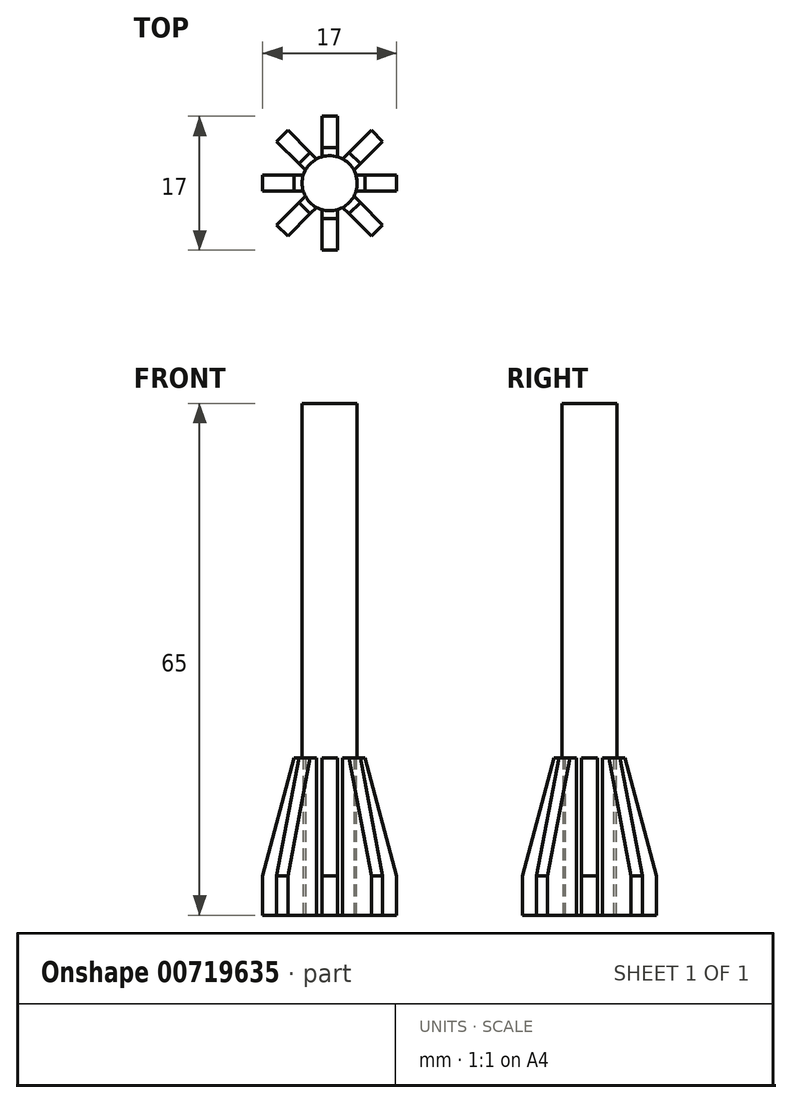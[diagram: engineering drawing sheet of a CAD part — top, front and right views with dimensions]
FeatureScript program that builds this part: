
annotation { "Feature Type Name" : "Feature", "Feature Type Description" : "" }
export const myFeature = defineFeature(function(context is Context, id is Id, definition is map)
    precondition{}
    {
        {
            var Q0;
            Q0=qCreatedBy(makeId("Top.planeOp"),FACE);
            var sketch = newSketch(context, id + "F0", { "sketchPlane" : qUnion([Q0])});
            skLineSegment(sketch, "E0.bottom", {"start": v(4.78, 10.23) * mm, "end": v(-7.24, -1.79) * mm});
            skLineSegment(sketch, "E0.top", {"start": v(6.2, 8.82) * mm, "end": v(-5.83, -3.2) * mm});
            skLineSegment(sketch, "E0.left", {"start": v(4.78, 10.23) * mm, "end": v(6.2, 8.82) * mm});
            skLineSegment(sketch, "E0.right", {"start": v(-7.24, -1.79) * mm, "end": v(-5.83, -3.2) * mm});
            skPoint(sketch, "E0.middle", {"position": v(-0.52, 3.52) * mm});
            skLineSegment(sketch, "E1.bottom", {"start": v(-5.83, 10.23) * mm, "end": v(-7.24, 8.82) * mm});
            skLineSegment(sketch, "E1.top", {"start": v(6.2, -1.79) * mm, "end": v(4.78, -3.2) * mm});
            skLineSegment(sketch, "E1.left", {"start": v(-5.83, 10.23) * mm, "end": v(6.2, -1.79) * mm});
            skLineSegment(sketch, "E1.right", {"start": v(-7.24, 8.82) * mm, "end": v(4.78, -3.2) * mm});
            skCircle(sketch, "E2", {"center": v(-0.52, 3.52) * mm, "radius": 3.5 * mm});
            skLineSegment(sketch, "E3.bottom", {"start": v(0.48, 12.02) * mm, "end": v(-1.52, 12.02) * mm});
            skLineSegment(sketch, "E3.top", {"start": v(0.48, -4.98) * mm, "end": v(-1.52, -4.98) * mm});
            skLineSegment(sketch, "E3.left", {"start": v(0.48, 12.02) * mm, "end": v(0.48, -4.98) * mm});
            skLineSegment(sketch, "E3.right", {"start": v(-1.52, 12.02) * mm, "end": v(-1.52, -4.98) * mm});
            skLineSegment(sketch, "E4.bottom", {"start": v(7.98, 4.52) * mm, "end": v(-9.02, 4.52) * mm});
            skLineSegment(sketch, "E4.top", {"start": v(7.98, 2.52) * mm, "end": v(-9.02, 2.52) * mm});
            skLineSegment(sketch, "E4.left", {"start": v(7.98, 4.52) * mm, "end": v(7.98, 2.52) * mm});
            skLineSegment(sketch, "E4.right", {"start": v(-9.02, 4.52) * mm, "end": v(-9.02, 2.52) * mm});
            skSolve(sketch);
        }
        {
            var Q0;
            {var subQ0=sQuery(id+"F0.wireOp",EDGE,"E2");var subQ1=sQuery(id+"F0.wireOp",EDGE,"E0.bottom");var subQ2=makeQuery(id+"F0.imprint","INTERSECT",VERTEX,{"disambiguationData":[OD(0.0)],"derivedFrom":[subQ1,subQ0]});Q0=makeQuery(id+"F0.imprint","IMPRINT",FACE,{"disambiguationData":[TD([[makeQuery(id+"F0.imprint","IMPRINT",EDGE,{"disambiguationData":[TD([[subQ2,-1.0]])],"derivedFrom":subQ1}),-1.0]])]});}
            var Q1;
            {var subQ0=sQuery(id+"F0.wireOp",EDGE,"E2");var subQ1=sQuery(id+"F0.wireOp",EDGE,"E0.bottom");var subQ2=makeQuery(id+"F0.imprint","INTERSECT",VERTEX,{"disambiguationData":[OD(1.0)],"derivedFrom":[subQ1,subQ0]});Q1=makeQuery(id+"F0.imprint","IMPRINT",FACE,{"disambiguationData":[TD([[makeQuery(id+"F0.imprint","IMPRINT",EDGE,{"disambiguationData":[TD([[subQ2,1.0]])],"derivedFrom":subQ1}),-1.0]])]});}
            var Q2;
            {var subQ0=sQuery(id+"F0.wireOp",EDGE,"E2");var subQ1=sQuery(id+"F0.wireOp",EDGE,"E0.top");var subQ2=makeQuery(id+"F0.imprint","INTERSECT",VERTEX,{"disambiguationData":[OD(0.0)],"derivedFrom":[subQ1,subQ0]});Q2=makeQuery(id+"F0.imprint","IMPRINT",FACE,{"disambiguationData":[TD([[makeQuery(id+"F0.imprint","IMPRINT",EDGE,{"disambiguationData":[TD([[subQ2,-1.0]])],"derivedFrom":subQ1}),1.0]])]});}
            var Q3;
            {var subQ0=sQuery(id+"F0.wireOp",EDGE,"E2");var subQ1=sQuery(id+"F0.wireOp",EDGE,"E0.top");var subQ2=makeQuery(id+"F0.imprint","INTERSECT",VERTEX,{"disambiguationData":[OD(1.0)],"derivedFrom":[subQ1,subQ0]});Q3=makeQuery(id+"F0.imprint","IMPRINT",FACE,{"disambiguationData":[TD([[makeQuery(id+"F0.imprint","IMPRINT",EDGE,{"disambiguationData":[TD([[subQ2,1.0]])],"derivedFrom":subQ1}),1.0]])]});}
            var Q4;
            {var subQ1=sQuery(id+"F0.wireOp",EDGE,"E0.bottom");var subQ5=sQuery(id+"F0.wireOp",EDGE,"E2");var subQ6=makeQuery(id+"F0.imprint","INTERSECT",VERTEX,{"disambiguationData":[OD(0.0)],"derivedFrom":[subQ1,subQ5]});Q4=makeQuery(id+"F0.imprint","IMPRINT",FACE,{"disambiguationData":[TD([[makeQuery(id+"F0.imprint","IMPRINT",EDGE,{"disambiguationData":[TD([[subQ6,-1.0]])],"derivedFrom":subQ1}),1.0]])]});}
            var Q5;
            {var subQ0=sQuery(id+"F0.wireOp",EDGE,"E1.left");var subQ1=sQuery(id+"F0.wireOp",EDGE,"E0.bottom");var subQ2=makeQuery(id+"F0.imprint","INTERSECT",VERTEX,{"derivedFrom":[subQ1,subQ0]});Q5=makeQuery(id+"F0.imprint","IMPRINT",FACE,{"disambiguationData":[TD([[makeQuery(id+"F0.imprint","IMPRINT",EDGE,{"disambiguationData":[TD([[subQ2,-1.0]])],"derivedFrom":subQ1}),-1.0]])]});}
            var Q6;
            {var subQ5=sQuery(id+"F0.wireOp",EDGE,"E2");var subQ6=sQuery(id+"F0.wireOp",EDGE,"E0.bottom");var subQ7=makeQuery(id+"F0.imprint","INTERSECT",VERTEX,{"disambiguationData":[OD(1.0)],"derivedFrom":[subQ6,subQ5]});Q6=makeQuery(id+"F0.imprint","IMPRINT",FACE,{"disambiguationData":[TD([[makeQuery(id+"F0.imprint","IMPRINT",EDGE,{"disambiguationData":[TD([[subQ7,1.0]])],"derivedFrom":subQ6}),1.0]])]});}
            var Q7;
            {var subQ0=sQuery(id+"F0.wireOp",EDGE,"E1.left");var subQ1=sQuery(id+"F0.wireOp",EDGE,"E0.top");var subQ2=makeQuery(id+"F0.imprint","INTERSECT",VERTEX,{"derivedFrom":[subQ1,subQ0]});Q7=makeQuery(id+"F0.imprint","IMPRINT",FACE,{"disambiguationData":[TD([[makeQuery(id+"F0.imprint","IMPRINT",EDGE,{"disambiguationData":[TD([[subQ2,-1.0]])],"derivedFrom":subQ1}),1.0]])]});}
            var Q8;
            {var subQ0=sQuery(id+"F0.wireOp",EDGE,"E1.left");var subQ1=sQuery(id+"F0.wireOp",EDGE,"E0.bottom");var subQ2=makeQuery(id+"F0.imprint","INTERSECT",VERTEX,{"derivedFrom":[subQ1,subQ0]});Q8=makeQuery(id+"F0.imprint","IMPRINT",FACE,{"disambiguationData":[TD([[makeQuery(id+"F0.imprint","IMPRINT",EDGE,{"disambiguationData":[TD([[subQ2,-1.0]])],"derivedFrom":subQ1}),1.0]])]});}
            var Q9;
            {var subQ1=sQuery(id+"F0.wireOp",EDGE,"E1.left");var subQ5=sQuery(id+"F0.wireOp",EDGE,"E2");var subQ9=makeQuery(id+"F0.imprint","INTERSECT",VERTEX,{"disambiguationData":[OD(0.0)],"derivedFrom":[subQ1,subQ5]});Q9=makeQuery(id+"F0.imprint","IMPRINT",FACE,{"disambiguationData":[TD([[makeQuery(id+"F0.imprint","IMPRINT",EDGE,{"disambiguationData":[TD([[subQ9,-1.0]])],"derivedFrom":subQ1}),-1.0]])]});}
            var Q10;
            {var subQ0=sQuery(id+"F0.wireOp",EDGE,"E3.left");var subQ1=sQuery(id+"F0.wireOp",EDGE,"E0.top");var subQ2=makeQuery(id+"F0.imprint","INTERSECT",VERTEX,{"derivedFrom":[subQ1,subQ0]});Q10=makeQuery(id+"F0.imprint","IMPRINT",FACE,{"disambiguationData":[TD([[makeQuery(id+"F0.imprint","IMPRINT",EDGE,{"disambiguationData":[TD([[subQ2,-1.0]])],"derivedFrom":subQ1}),1.0]])]});}
            var Q11;
            {var subQ5=sQuery(id+"F0.wireOp",EDGE,"E1.right");var subQ7=sQuery(id+"F0.wireOp",EDGE,"E0.bottom");var subQ8=makeQuery(id+"F0.imprint","INTERSECT",VERTEX,{"derivedFrom":[subQ7,subQ5]});Q11=makeQuery(id+"F0.imprint","IMPRINT",FACE,{"disambiguationData":[TD([[makeQuery(id+"F0.imprint","IMPRINT",EDGE,{"disambiguationData":[TD([[subQ8,-1.0]])],"derivedFrom":subQ7}),-1.0]])]});}
            var Q12;
            {var subQ0=sQuery(id+"F0.wireOp",EDGE,"E3.left");var subQ5=sQuery(id+"F0.wireOp",EDGE,"E0.bottom");var subQ6=makeQuery(id+"F0.imprint","INTERSECT",VERTEX,{"derivedFrom":[subQ5,subQ0]});Q12=makeQuery(id+"F0.imprint","IMPRINT",FACE,{"disambiguationData":[TD([[makeQuery(id+"F0.imprint","IMPRINT",EDGE,{"disambiguationData":[TD([[subQ6,-1.0]])],"derivedFrom":subQ5}),-1.0]])]});}
            var Q13;
            {var subQ0=sQuery(id+"F0.wireOp",EDGE,"E4.bottom");var subQ3=sQuery(id+"F0.wireOp",EDGE,"E0.top");var subQ4=makeQuery(id+"F0.imprint","INTERSECT",VERTEX,{"derivedFrom":[subQ3,subQ0]});Q13=makeQuery(id+"F0.imprint","IMPRINT",FACE,{"disambiguationData":[TD([[makeQuery(id+"F0.imprint","IMPRINT",EDGE,{"disambiguationData":[TD([[subQ4,-1.0]])],"derivedFrom":subQ3}),1.0]])]});}
            var Q14;
            {var subQ0=sQuery(id+"F0.wireOp",EDGE,"E3.right");var subQ1=sQuery(id+"F0.wireOp",EDGE,"E0.bottom");var subQ2=makeQuery(id+"F0.imprint","INTERSECT",VERTEX,{"derivedFrom":[subQ1,subQ0]});Q14=makeQuery(id+"F0.imprint","IMPRINT",FACE,{"disambiguationData":[TD([[makeQuery(id+"F0.imprint","IMPRINT",EDGE,{"disambiguationData":[TD([[subQ2,-1.0]])],"derivedFrom":subQ1}),1.0]])]});}
            var Q15;
            {var subQ0=sQuery(id+"F0.wireOp",EDGE,"E3.left");var subQ1=sQuery(id+"F0.wireOp",EDGE,"E0.bottom");var subQ2=makeQuery(id+"F0.imprint","INTERSECT",VERTEX,{"derivedFrom":[subQ1,subQ0]});Q15=makeQuery(id+"F0.imprint","IMPRINT",FACE,{"disambiguationData":[TD([[makeQuery(id+"F0.imprint","IMPRINT",EDGE,{"disambiguationData":[TD([[subQ2,-1.0]])],"derivedFrom":subQ1}),1.0]])]});}
            var Q16;
            {var subQ0=sQuery(id+"F0.wireOp",EDGE,"E4.bottom");var subQ1=sQuery(id+"F0.wireOp",EDGE,"E0.bottom");var subQ2=makeQuery(id+"F0.imprint","INTERSECT",VERTEX,{"derivedFrom":[subQ1,subQ0]});Q16=makeQuery(id+"F0.imprint","IMPRINT",FACE,{"disambiguationData":[TD([[makeQuery(id+"F0.imprint","IMPRINT",EDGE,{"disambiguationData":[TD([[subQ2,-1.0]])],"derivedFrom":subQ1}),-1.0]])]});}
            var Q17;
            {var subQ0=sQuery(id+"F0.wireOp",EDGE,"E2");var subQ1=sQuery(id+"F0.wireOp",EDGE,"E1.left");var subQ2=makeQuery(id+"F0.imprint","INTERSECT",VERTEX,{"disambiguationData":[OD(1.0)],"derivedFrom":[subQ1,subQ0]});Q17=makeQuery(id+"F0.imprint","IMPRINT",FACE,{"disambiguationData":[TD([[makeQuery(id+"F0.imprint","IMPRINT",EDGE,{"disambiguationData":[TD([[subQ2,1.0]])],"derivedFrom":subQ1}),-1.0]])]});}
            var Q18;
            {var subQ0=sQuery(id+"F0.wireOp",EDGE,"E1.left");var subQ1=sQuery(id+"F0.wireOp",EDGE,"E0.top");var subQ2=makeQuery(id+"F0.imprint","INTERSECT",VERTEX,{"derivedFrom":[subQ1,subQ0]});Q18=makeQuery(id+"F0.imprint","IMPRINT",FACE,{"disambiguationData":[TD([[makeQuery(id+"F0.imprint","IMPRINT",EDGE,{"disambiguationData":[TD([[subQ2,-1.0]])],"derivedFrom":subQ1}),-1.0]])]});}
            var Q19;
            {var subQ9=sQuery(id+"F0.wireOp",EDGE,"E4.bottom");var subQ13=sQuery(id+"F0.wireOp",EDGE,"E0.bottom");var subQ14=makeQuery(id+"F0.imprint","INTERSECT",VERTEX,{"derivedFrom":[subQ13,subQ9]});Q19=makeQuery(id+"F0.imprint","IMPRINT",FACE,{"disambiguationData":[TD([[makeQuery(id+"F0.imprint","IMPRINT",EDGE,{"disambiguationData":[TD([[subQ14,-1.0]])],"derivedFrom":subQ13}),1.0]])]});}
            var Q20;
            {var subQ0=sQuery(id+"F0.wireOp",EDGE,"E2");var subQ1=sQuery(id+"F0.wireOp",EDGE,"E1.left");var subQ2=makeQuery(id+"F0.imprint","INTERSECT",VERTEX,{"disambiguationData":[OD(1.0)],"derivedFrom":[subQ1,subQ0]});Q20=makeQuery(id+"F0.imprint","IMPRINT",FACE,{"disambiguationData":[TD([[makeQuery(id+"F0.imprint","IMPRINT",EDGE,{"disambiguationData":[TD([[subQ2,1.0]])],"derivedFrom":subQ1}),1.0]])]});}
            var Q21;
            {var subQ0=sQuery(id+"F0.wireOp",EDGE,"E4.bottom");var subQ1=sQuery(id+"F0.wireOp",EDGE,"E1.left");var subQ2=makeQuery(id+"F0.imprint","INTERSECT",VERTEX,{"derivedFrom":[subQ1,subQ0]});Q21=makeQuery(id+"F0.imprint","IMPRINT",FACE,{"disambiguationData":[TD([[makeQuery(id+"F0.imprint","IMPRINT",EDGE,{"disambiguationData":[TD([[subQ2,-1.0]])],"derivedFrom":subQ1}),1.0]])]});}
            var Q22;
            {var subQ0=sQuery(id+"F0.wireOp",EDGE,"E3.right");var subQ1=sQuery(id+"F0.wireOp",EDGE,"E0.bottom");var subQ2=makeQuery(id+"F0.imprint","INTERSECT",VERTEX,{"derivedFrom":[subQ1,subQ0]});Q22=makeQuery(id+"F0.imprint","IMPRINT",FACE,{"disambiguationData":[TD([[makeQuery(id+"F0.imprint","IMPRINT",EDGE,{"disambiguationData":[TD([[subQ2,-1.0]])],"derivedFrom":subQ1}),-1.0]])]});}
            var Q23;
            {var subQ5=sQuery(id+"F0.wireOp",EDGE,"E1.right");var subQ6=sQuery(id+"F0.wireOp",EDGE,"E0.top");var subQ7=makeQuery(id+"F0.imprint","INTERSECT",VERTEX,{"derivedFrom":[subQ6,subQ5]});Q23=makeQuery(id+"F0.imprint","IMPRINT",FACE,{"disambiguationData":[TD([[makeQuery(id+"F0.imprint","IMPRINT",EDGE,{"disambiguationData":[TD([[subQ7,-1.0]])],"derivedFrom":subQ6}),1.0]])]});}
            var Q24;
            {var subQ0=sQuery(id+"F0.wireOp",EDGE,"E2");var subQ1=sQuery(id+"F0.wireOp",EDGE,"E1.left");var subQ2=makeQuery(id+"F0.imprint","INTERSECT",VERTEX,{"disambiguationData":[OD(0.0)],"derivedFrom":[subQ1,subQ0]});Q24=makeQuery(id+"F0.imprint","IMPRINT",FACE,{"disambiguationData":[TD([[makeQuery(id+"F0.imprint","IMPRINT",EDGE,{"disambiguationData":[TD([[subQ2,-1.0]])],"derivedFrom":subQ1}),1.0]])]});}
            var Q25;
            {var subQ0=sQuery(id+"F0.wireOp",EDGE,"E1.right");var subQ1=sQuery(id+"F0.wireOp",EDGE,"E0.bottom");var subQ2=makeQuery(id+"F0.imprint","INTERSECT",VERTEX,{"derivedFrom":[subQ1,subQ0]});Q25=makeQuery(id+"F0.imprint","IMPRINT",FACE,{"disambiguationData":[TD([[makeQuery(id+"F0.imprint","IMPRINT",EDGE,{"disambiguationData":[TD([[subQ2,-1.0]])],"derivedFrom":subQ1}),1.0]])]});}
            var Q26;
            {var subQ0=sQuery(id+"F0.wireOp",EDGE,"E2");var subQ1=sQuery(id+"F0.wireOp",EDGE,"E1.right");var subQ2=makeQuery(id+"F0.imprint","INTERSECT",VERTEX,{"disambiguationData":[OD(0.0)],"derivedFrom":[subQ1,subQ0]});Q26=makeQuery(id+"F0.imprint","IMPRINT",FACE,{"disambiguationData":[TD([[makeQuery(id+"F0.imprint","IMPRINT",EDGE,{"disambiguationData":[TD([[subQ2,-1.0]])],"derivedFrom":subQ1}),-1.0]])]});}
            var Q27;
            {var subQ0=sQuery(id+"F0.wireOp",EDGE,"E3.right");var subQ1=sQuery(id+"F0.wireOp",EDGE,"E1.right");var subQ2=makeQuery(id+"F0.imprint","INTERSECT",VERTEX,{"derivedFrom":[subQ1,subQ0]});Q27=makeQuery(id+"F0.imprint","IMPRINT",FACE,{"disambiguationData":[TD([[makeQuery(id+"F0.imprint","IMPRINT",EDGE,{"disambiguationData":[TD([[subQ2,-1.0]])],"derivedFrom":subQ1}),-1.0]])]});}
            var Q28;
            {var subQ0=sQuery(id+"F0.wireOp",EDGE,"E1.right");var subQ1=sQuery(id+"F0.wireOp",EDGE,"E0.top");var subQ2=makeQuery(id+"F0.imprint","INTERSECT",VERTEX,{"derivedFrom":[subQ1,subQ0]});Q28=makeQuery(id+"F0.imprint","IMPRINT",FACE,{"disambiguationData":[TD([[makeQuery(id+"F0.imprint","IMPRINT",EDGE,{"disambiguationData":[TD([[subQ2,-1.0]])],"derivedFrom":subQ1}),-1.0]])]});}
            var Q29;
            {var subQ0=sQuery(id+"F0.wireOp",EDGE,"E4.top");var subQ1=sQuery(id+"F0.wireOp",EDGE,"E0.top");var subQ2=makeQuery(id+"F0.imprint","INTERSECT",VERTEX,{"derivedFrom":[subQ1,subQ0]});Q29=makeQuery(id+"F0.imprint","IMPRINT",FACE,{"disambiguationData":[TD([[makeQuery(id+"F0.imprint","IMPRINT",EDGE,{"disambiguationData":[TD([[subQ2,-1.0]])],"derivedFrom":subQ1}),-1.0]])]});}
            var Q30;
            {var subQ0=sQuery(id+"F0.wireOp",EDGE,"E4.top");var subQ1=sQuery(id+"F0.wireOp",EDGE,"E0.top");var subQ2=makeQuery(id+"F0.imprint","INTERSECT",VERTEX,{"derivedFrom":[subQ1,subQ0]});Q30=makeQuery(id+"F0.imprint","IMPRINT",FACE,{"disambiguationData":[TD([[makeQuery(id+"F0.imprint","IMPRINT",EDGE,{"disambiguationData":[TD([[subQ2,-1.0]])],"derivedFrom":subQ1}),1.0]])]});}
            var Q31;
            {var subQ0=sQuery(id+"F0.wireOp",EDGE,"E4.bottom");var subQ1=sQuery(id+"F0.wireOp",EDGE,"E0.top");var subQ2=makeQuery(id+"F0.imprint","INTERSECT",VERTEX,{"derivedFrom":[subQ1,subQ0]});Q31=makeQuery(id+"F0.imprint","IMPRINT",FACE,{"disambiguationData":[TD([[makeQuery(id+"F0.imprint","IMPRINT",EDGE,{"disambiguationData":[TD([[subQ2,-1.0]])],"derivedFrom":subQ1}),-1.0]])]});}
            var Q32;
            {var subQ0=sQuery(id+"F0.wireOp",EDGE,"E2");var subQ1=sQuery(id+"F0.wireOp",EDGE,"E1.right");var subQ2=makeQuery(id+"F0.imprint","INTERSECT",VERTEX,{"disambiguationData":[OD(1.0)],"derivedFrom":[subQ1,subQ0]});Q32=makeQuery(id+"F0.imprint","IMPRINT",FACE,{"disambiguationData":[TD([[makeQuery(id+"F0.imprint","IMPRINT",EDGE,{"disambiguationData":[TD([[subQ2,1.0]])],"derivedFrom":subQ1}),-1.0]])]});}
            extrude(context, id + "F1", {"entities" : qUnion([Q0, Q1, Q2, Q3, Q4, Q5, Q6, Q7, Q8, Q9, Q10, Q11, Q12, Q13, Q14, Q15, Q16, Q17, Q18, Q19, Q20, Q21, Q22, Q23, Q24, Q25, Q26, Q27, Q28, Q29, Q30, Q31, Q32]), "depth" : 65 * mm, "offsetDistance" : 25 * mm});
        }
        {
            var Q0;
            {var subQ0=sQuery(id+"F0.wireOp",EDGE,"E0.left");Q0=makeQuery(id+"F0.imprint","IMPRINT",FACE,{"disambiguationData":[TD([[makeQuery(id+"F0.imprint","IMPRINT",EDGE,{"derivedFrom":subQ0}),-1.0]])]});}
            var Q1;
            {var subQ0=sQuery(id+"F0.wireOp",EDGE,"E1.bottom");Q1=makeQuery(id+"F0.imprint","IMPRINT",FACE,{"disambiguationData":[TD([[makeQuery(id+"F0.imprint","IMPRINT",EDGE,{"derivedFrom":subQ0}),1.0]])]});}
            var Q2;
            {var subQ0=sQuery(id+"F0.wireOp",EDGE,"E0.right");Q2=makeQuery(id+"F0.imprint","IMPRINT",FACE,{"disambiguationData":[TD([[makeQuery(id+"F0.imprint","IMPRINT",EDGE,{"derivedFrom":subQ0}),1.0]])]});}
            var Q3;
            {var subQ5=sQuery(id+"F0.wireOp",EDGE,"E4.right");Q3=makeQuery(id+"F0.imprint","IMPRINT",FACE,{"disambiguationData":[TD([[makeQuery(id+"F0.imprint","IMPRINT",EDGE,{"derivedFrom":subQ5}),1.0]])]});}
            var Q4;
            {var subQ5=sQuery(id+"F0.wireOp",EDGE,"E3.top");Q4=makeQuery(id+"F0.imprint","IMPRINT",FACE,{"disambiguationData":[TD([[makeQuery(id+"F0.imprint","IMPRINT",EDGE,{"derivedFrom":subQ5}),-1.0]])]});}
            var Q5;
            {var subQ5=sQuery(id+"F0.wireOp",EDGE,"E4.left");Q5=makeQuery(id+"F0.imprint","IMPRINT",FACE,{"disambiguationData":[TD([[makeQuery(id+"F0.imprint","IMPRINT",EDGE,{"derivedFrom":subQ5}),-1.0]])]});}
            var Q6;
            {var subQ0=sQuery(id+"F0.wireOp",EDGE,"E1.top");Q6=makeQuery(id+"F0.imprint","IMPRINT",FACE,{"disambiguationData":[TD([[makeQuery(id+"F0.imprint","IMPRINT",EDGE,{"derivedFrom":subQ0}),-1.0]])]});}
            var Q7;
            {var subQ5=sQuery(id+"F0.wireOp",EDGE,"E3.bottom");Q7=makeQuery(id+"F0.imprint","IMPRINT",FACE,{"disambiguationData":[TD([[makeQuery(id+"F0.imprint","IMPRINT",EDGE,{"derivedFrom":subQ5}),1.0]])]});}
            extrude(context, id + "F2", {"entities" : qUnion([Q0, Q1, Q2, Q3, Q4, Q5, Q6, Q7]), "operationType" : NewBodyOperationType.ADD, "depth" : 20 * mm, "offsetDistance" : 25 * mm});
        }
        {
            var Q0;
            Q0=makeQuery(id+"F2.opExtrude","CAP_EDGE",EDGE,{"disambiguationData":[OSD([sQuery(id+"F0.wireOp",EDGE,"E1.bottom")])],"isStart":false});
            var Q1;
            Q1=makeQuery(id+"F2.opExtrude","CAP_EDGE",EDGE,{"disambiguationData":[OSD([sQuery(id+"F0.wireOp",EDGE,"E0.right")])],"isStart":false});
            var Q2;
            Q2=makeQuery(id+"F2.opExtrude","CAP_EDGE",EDGE,{"disambiguationData":[OSD([sQuery(id+"F0.wireOp",EDGE,"E3.bottom")])],"isStart":false});
            var Q3;
            Q3=makeQuery(id+"F2.opExtrude","CAP_EDGE",EDGE,{"disambiguationData":[OSD([sQuery(id+"F0.wireOp",EDGE,"E4.right")])],"isStart":false});
            chamfer(context, id + "F3", {"entities" : qUnion([Q0, Q1, Q2, Q3]), "chamferType" : ChamferType.TWO_OFFSETS, "width1" : 4 * mm, "oppositeDirection" : false, "width2" : 15 * mm, "tangentPropagation" : true});
        }
        {
            var Q0;
            Q0=makeQuery(id+"F2.opExtrude","CAP_EDGE",EDGE,{"disambiguationData":[OSD([sQuery(id+"F0.wireOp",EDGE,"E1.top")])],"isStart":false});
            var Q1;
            Q1=makeQuery(id+"F2.opExtrude","CAP_EDGE",EDGE,{"disambiguationData":[OSD([sQuery(id+"F0.wireOp",EDGE,"E0.left")])],"isStart":false});
            var Q2;
            Q2=makeQuery(id+"F2.opExtrude","CAP_EDGE",EDGE,{"disambiguationData":[OSD([sQuery(id+"F0.wireOp",EDGE,"E3.top")])],"isStart":false});
            var Q3;
            Q3=makeQuery(id+"F2.opExtrude","CAP_EDGE",EDGE,{"disambiguationData":[OSD([sQuery(id+"F0.wireOp",EDGE,"E4.left")])],"isStart":false});
            chamfer(context, id + "F4", {"entities" : qUnion([Q0, Q1, Q2, Q3]), "chamferType" : ChamferType.TWO_OFFSETS, "width1" : 15 * mm, "oppositeDirection" : false, "width2" : 4 * mm, "tangentPropagation" : true});
        }
    });
